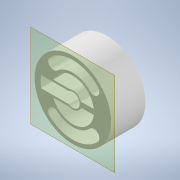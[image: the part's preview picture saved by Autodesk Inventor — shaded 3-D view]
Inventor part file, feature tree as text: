
AUTODESK INVENTOR PART (.ipt)
format: ipt  version: 2020 (Build 240168000, 168)  size: 145,920 bytes
history: native  units: mm
features: plane x2, other x2, extrude x1, sketch x1, reference x1
ambient origin geometry x8: Origin, YZ Plane, XZ Plane, XY Plane, X Axis, Y Axis, Z Axis, Center Point
bodies: Solid1 (feature_tree)
feature tree (7):
  plane  "Work Plane1"
  extrude  "Extrusion1"  [1 undecoded]
  plane  "Work Plane2"
  sketch  "Sketch1"  dims[d0=14.75mm d1=0.0mm]
  reference  "Reference1"
  other  "Assembly1"
  other  "pillen_drummer:1"
note: 1 required parameter value undecoded (feature->parameter linkage not recoverable at this tier; creation-order binding heuristic only, values carry confidence <= 0.55)
